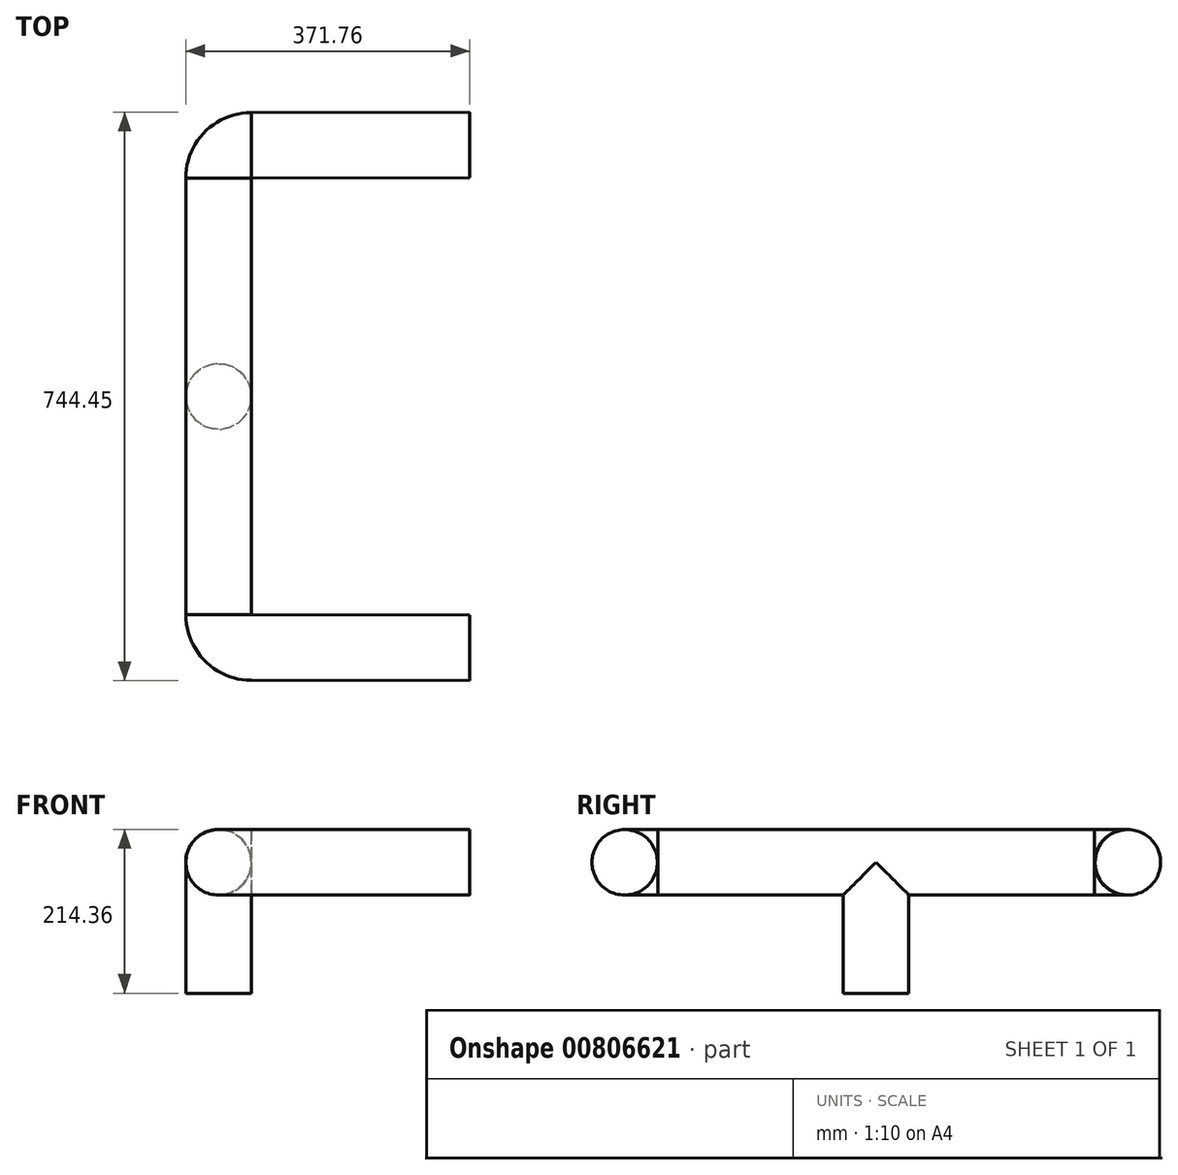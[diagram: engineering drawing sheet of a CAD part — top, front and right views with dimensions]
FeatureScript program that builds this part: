
annotation { "Feature Type Name" : "Feature", "Feature Type Description" : "" }
export const myFeature = defineFeature(function(context is Context, id is Id, definition is map)
    precondition{}
    {
        {
            var Q0;
            Q0=qCreatedBy(makeId("Top.planeOp"),FACE);
            var sketch = newSketch(context, id + "F0", { "sketchPlane" : qUnion([Q0])});
            skCircle(sketch, "E0", {"center": v(0, 0) * mm, "radius": 76.2 * mm});
            skSolve(sketch);
        }
        {
            var Q0;
            Q0=makeQuery(id+"F0.imprint","IMPRINT",FACE,{"disambiguationData":[TD([[makeQuery(id+"F0.imprint","IMPRINT",EDGE,{"derivedFrom":sQuery(id+"F0.wireOp",EDGE,"E0")}),1.0]])]});
            extrude(context, id + "F1", {"entities" : qUnion([Q0]), "depth" : 304.8 * mm, "offsetDistance" : 25.4 * mm});
        }
        {
            var Q0;
            Q0=makeQuery(id+"F1.opExtrude","CAP_FACE",FACE,{"disambiguationData":[OSD([sQuery(id+"F0.wireOp",EDGE,"E0")])],"isStart":false});
            var sketch = newSketch(context, id + "F2", { "sketchPlane" : qUnion([Q0])});
            skLineSegment(sketch, "E1", {"start": v(0, 0) * mm, "end": v(0, -508) * mm});
            skSolve(sketch);
        }
        {
            var Q0;
            Q0=makeQuery(id+"F2.imprint","IMPRINT",FACE,{"disambiguationData":[TD([[makeQuery(id+"F2.imprint","IMPRINT",EDGE,{"derivedFrom":makeQuery(id+"F1.opExtrude","CAP_EDGE",EDGE,{"disambiguationData":[OSD([sQuery(id+"F0.wireOp",EDGE,"E0")])],"isStart":false})}),1.0]])]});
            var sketch = newSketch(context, id + "F3", { "sketchPlane" : qUnion([Q0])});
            skLineSegment(sketch, "E2", {"start": v(0, 0) * mm, "end": v(0, 508) * mm});
            skSolve(sketch);
        }
        {
            var Q0;
            Q0=sQuery(id+"F2.wireOp",VERTEX,"E1.end");
            var Q1;
            Q1=sQuery(id+"F2.wireOp",EDGE,"E1");
            cPlane(context, id + "F4", {"entities" : qUnion([Q0, Q1]), "cplaneType" : CPlaneType.LINE_POINT, "offset" : 25.4 * mm, "width" : 152.4 * mm, "height" : 152.4 * mm});
        }
        {
            var Q0;
            Q0=qCreatedBy(id+"F4.planeOp",FACE);
            var sketch = newSketch(context, id + "F5", { "sketchPlane" : qUnion([Q0])});
            skPoint(sketch, "E3", {"position": v(0, 304.8) * mm});
            skSolve(sketch);
        }
        {
            var Q0;
            Q0=qCreatedBy(id+"F4.planeOp",FACE);
            var sketch = newSketch(context, id + "F6", { "sketchPlane" : qUnion([Q0])});
            skCircle(sketch, "E4", {"center": v(0, 304.89) * mm, "radius": 76.2 * mm});
            skSolve(sketch);
        }
        {
            var Q0;
            Q0=makeQuery(id+"F6.imprint","IMPRINT",FACE,{"disambiguationData":[TD([[makeQuery(id+"F6.imprint","IMPRINT",EDGE,{"derivedFrom":sQuery(id+"F6.wireOp",EDGE,"E4")}),1.0]])]});
            var Q1;
            Q1=sQuery(id+"F2.wireOp",EDGE,"E1");
            var Q2;
            Q2=sQuery(id+"F3.wireOp",EDGE,"E2");
            sweep(context, id + "F7", {"operationType" : NewBodyOperationType.ADD, "profiles" : qUnion([Q0]), "path" : qUnion([Q1, Q2])});
        }
        {
            var Q0;
            Q0=makeQuery(id+"F7.opSweep","CAP_FACE",FACE,{"disambiguationData":[OSD([sQuery(id+"F2.wireOp",VERTEX,"E1.end"),sQuery(id+"F6.wireOp",EDGE,"E4")])],"isStart":true});
            var sketch = newSketch(context, id + "F8", { "sketchPlane" : qUnion([Q0])});
            skLineSegment(sketch, "E5", {"start": v(0, 304.89) * mm, "end": v(0, 228.69) * mm});
            skSolve(sketch);
        }
        {
            var Q0;
            Q0=sQuery(id+"F8.wireOp",EDGE,"E5");
            var Q1;
            Q1=sQuery(id+"F5.wireOp",VERTEX,"E3");
            cPlane(context, id + "F9", {"entities" : qUnion([Q0, Q1]), "cplaneType" : CPlaneType.LINE_POINT, "offset" : 25.4 * mm, "width" : 152.4 * mm, "height" : 152.4 * mm});
        }
        {
            var Q0;
            Q0=qCreatedBy(id+"F9.planeOp",FACE);
            var sketch = newSketch(context, id + "F10", { "sketchPlane" : qUnion([Q0])});
            skArc(sketch, "E6", {"start": v(76.2, 584.23) * mm, "mid": v(22.4, 561.9) * mm, "end": v(0.07, 508.08) * mm});
            skSolve(sketch);
        }
        {
            var Q0;
            Q0=sQuery(id+"F10.wireOp",EDGE,"E6");
            var Q1;
            Q1=sQuery(id+"F10.wireOp",VERTEX,"E6.start");
            cPlane(context, id + "F11", {"entities" : qUnion([Q0, Q1]), "cplaneType" : CPlaneType.CURVE_POINT, "offset" : 25.4 * mm, "width" : 152.4 * mm, "height" : 152.4 * mm});
        }
        {
            var Q0;
            Q0=qCreatedBy(id+"F11.planeOp",FACE);
            var sketch = newSketch(context, id + "F12", { "sketchPlane" : qUnion([Q0])});
            skCircle(sketch, "E7", {"center": v(584.29, 304.8) * mm, "radius": 76.2 * mm});
            skSolve(sketch);
        }
        {
            var Q0;
            Q0=makeQuery(id+"F12.imprint","IMPRINT",FACE,{"disambiguationData":[TD([[makeQuery(id+"F12.imprint","IMPRINT",EDGE,{"derivedFrom":sQuery(id+"F12.wireOp",EDGE,"E7")}),1.0]])]});
            var Q1;
            Q1=sQuery(id+"F10.wireOp",EDGE,"E6");
            sweep(context, id + "F13", {"profiles" : qUnion([Q0]), "path" : qUnion([Q1])});
        }
        {
            var Q0;
            Q0=makeQuery(id+"F7.opSweep","CAP_FACE",FACE,{"disambiguationData":[OSD([sQuery(id+"F3.wireOp",VERTEX,"E2.end"),sQuery(id+"F6.wireOp",EDGE,"E4")])],"isStart":false});
            var sketch = newSketch(context, id + "F14", { "sketchPlane" : qUnion([Q0])});
            skPoint(sketch, "E8", {"position": v(0, 304.89) * mm});
            skSolve(sketch);
        }
        {
            var Q0;
            Q0=qCreatedBy(makeId("Right.planeOp"),FACE);
            var sketch = newSketch(context, id + "F15", { "sketchPlane" : qUnion([Q0])});
            skLineSegment(sketch, "E9", {"start": v(508.18, 305.03) * mm, "end": v(426.1, 305.03) * mm});
            skSolve(sketch);
        }
        {
            var Q0;
            Q0=sQuery(id+"F15.wireOp",EDGE,"E9");
            var Q1;
            Q1=sQuery(id+"F14.wireOp",VERTEX,"E8");
            cPlane(context, id + "F16", {"entities" : qUnion([Q0, Q1]), "cplaneType" : CPlaneType.LINE_POINT, "offset" : 25.4 * mm, "width" : 152.4 * mm, "height" : 152.4 * mm});
        }
        {
            var Q0;
            Q0=qCreatedBy(id+"F16.planeOp",FACE);
            var sketch = newSketch(context, id + "F17", { "sketchPlane" : qUnion([Q0])});
            skLineSegment(sketch, "E10", {"start": v(0, 306.54) * mm, "end": v(0, 229.61) * mm});
            skSolve(sketch);
        }
        {
            var Q0;
            Q0=sQuery(id+"F17.wireOp",EDGE,"E10");
            var Q1;
            Q1=sQuery(id+"F14.wireOp",VERTEX,"E8");
            cPlane(context, id + "F18", {"entities" : qUnion([Q0, Q1]), "cplaneType" : CPlaneType.LINE_POINT, "offset" : 25.4 * mm, "width" : 152.4 * mm, "height" : 152.4 * mm});
        }
        {
            var Q0;
            Q0=qCreatedBy(id+"F18.planeOp",FACE);
            var sketch = newSketch(context, id + "F19", { "sketchPlane" : qUnion([Q0])});
            skArc(sketch, "E11", {"start": v(0, -508.1) * mm, "mid": v(22.24, -561.88) * mm, "end": v(75.96, -584.27) * mm});
            skSolve(sketch);
        }
        {
            var Q0;
            Q0=sQuery(id+"F19.wireOp",EDGE,"E11");
            var Q1;
            Q1=sQuery(id+"F19.wireOp",VERTEX,"E11.end");
            cPlane(context, id + "F20", {"entities" : qUnion([Q0, Q1]), "cplaneType" : CPlaneType.CURVE_POINT, "offset" : 25.4 * mm, "width" : 152.4 * mm, "height" : 152.4 * mm});
        }
        {
            var Q0;
            Q0=qCreatedBy(id+"F20.planeOp",FACE);
            var sketch = newSketch(context, id + "F21", { "sketchPlane" : qUnion([Q0])});
            skCircle(sketch, "E12", {"center": v(584.46, 304.75) * mm, "radius": 76.2 * mm});
            skSolve(sketch);
        }
        {
            var Q0;
            Q0=makeQuery(id+"F21.imprint","IMPRINT",FACE,{"disambiguationData":[TD([[makeQuery(id+"F21.imprint","IMPRINT",EDGE,{"derivedFrom":sQuery(id+"F21.wireOp",EDGE,"E12")}),1.0]])]});
            var Q1;
            Q1=sQuery(id+"F19.wireOp",EDGE,"E11");
            sweep(context, id + "F22", {"profiles" : qUnion([Q0]), "path" : qUnion([Q1])});
        }
        {
            var Q0;
            Q0=makeQuery(id+"F13.opSweep","CAP_FACE",FACE,{"disambiguationData":[OSD([sQuery(id+"F10.wireOp",VERTEX,"E6.start"),sQuery(id+"F12.wireOp",EDGE,"E7")])],"isStart":true});
            var sketch = newSketch(context, id + "F23", { "sketchPlane" : qUnion([Q0])});
            skPoint(sketch, "E13", {"position": v(-584.29, 304.8) * mm});
            skSolve(sketch);
        }
        {
            var Q0;
            Q0=makeQuery(id+"F23.imprint","IMPRINT",FACE,{"disambiguationData":[TD([[makeQuery(id+"F23.imprint","IMPRINT",EDGE,{"derivedFrom":makeQuery(id+"F13.opSweep","CAP_EDGE",EDGE,{"disambiguationData":[OSD([sQuery(id+"F10.wireOp",VERTEX,"E6.start"),sQuery(id+"F12.wireOp",EDGE,"E7")])],"isStart":true})}),-1.0]])]});
            var sketch = newSketch(context, id + "F24", { "sketchPlane" : qUnion([Q0])});
            skCircle(sketch, "E14", {"center": v(-584.28, 304.81) * mm, "radius": 76.2 * mm});
            skSolve(sketch);
        }
        {
            var Q0;
            Q0 = qSketchRegion(id + "F24", true);
            extrude(context, id + "F25", {"entities" : qUnion([Q0]), "operationType" : NewBodyOperationType.ADD, "depth" : 508 * mm, "offsetDistance" : 25.4 * mm});
        }
        {
            var Q0;
            Q0=makeQuery(id+"F22.opSweep","CAP_FACE",FACE,{"disambiguationData":[OSD([sQuery(id+"F19.wireOp",VERTEX,"E11.end"),sQuery(id+"F21.wireOp",EDGE,"E12")])],"isStart":true});
            var sketch = newSketch(context, id + "F26", { "sketchPlane" : qUnion([Q0])});
            skPoint(sketch, "E15", {"position": v(584.46, 304.75) * mm});
            skSolve(sketch);
        }
        {
            var Q0;
            Q0=makeQuery(id+"F26.imprint","IMPRINT",FACE,{"disambiguationData":[TD([[makeQuery(id+"F26.imprint","IMPRINT",EDGE,{"derivedFrom":makeQuery(id+"F22.opSweep","CAP_EDGE",EDGE,{"disambiguationData":[OSD([sQuery(id+"F19.wireOp",VERTEX,"E11.end"),sQuery(id+"F21.wireOp",EDGE,"E12")])],"isStart":true})}),-1.0]])]});
            var sketch = newSketch(context, id + "F27", { "sketchPlane" : qUnion([Q0])});
            skCircle(sketch, "E16", {"center": v(584.45, 304.76) * mm, "radius": 76.2 * mm});
            skSolve(sketch);
        }
        {
            var Q0;
            Q0 = qSketchRegion(id + "F27", true);
            extrude(context, id + "F28", {"entities" : qUnion([Q0]), "operationType" : NewBodyOperationType.ADD, "depth" : 508 * mm, "offsetDistance" : 25.4 * mm});
        }
        {
            var Q0;
            Q0=makeQuery(id+"F13.opSweep","SWEPT_BODY",BODY,{"disambiguationData":[OSD([sQuery(id+"F10.wireOp",EDGE,"E6"),sQuery(id+"F12.wireOp",EDGE,"E7")])]});
            var Q1;
            Q1=makeQuery(id+"F1.opExtrude","SWEPT_BODY",BODY,{"disambiguationData":[OSD([sQuery(id+"F0.wireOp",EDGE,"E0")])]});
            var Q2;
            Q2=makeQuery(id+"F22.opSweep","SWEPT_BODY",BODY,{"disambiguationData":[OSD([sQuery(id+"F19.wireOp",EDGE,"E11"),sQuery(id+"F21.wireOp",EDGE,"E12")])]});
            var Q3;
            Q3=qCreatedBy(makeId("Origin.pointOp"),VERTEX);
            transform(context, id + "F29", {"entities" : qUnion([Q0, Q1, Q2]), "transformType" : TransformType.SCALE_UNIFORMLY, "scale" : .75, "scalePoint" : qUnion([Q3]), "makeCopy" : false});
        }
        {
            var Q0;
            Q0=makeQuery(id+"F13.opSweep","SWEPT_BODY",BODY,{"disambiguationData":[OSD([sQuery(id+"F10.wireOp",EDGE,"E6"),sQuery(id+"F12.wireOp",EDGE,"E7")])]});
            var Q1;
            Q1=makeQuery(id+"F1.opExtrude","SWEPT_BODY",BODY,{"disambiguationData":[OSD([sQuery(id+"F0.wireOp",EDGE,"E0")])]});
            var Q2;
            Q2=makeQuery(id+"F22.opSweep","SWEPT_BODY",BODY,{"disambiguationData":[OSD([sQuery(id+"F19.wireOp",EDGE,"E11"),sQuery(id+"F21.wireOp",EDGE,"E12")])]});
            var Q3;
            Q3=qCreatedBy(makeId("Origin.pointOp"),VERTEX);
            transform(context, id + "F30", {"entities" : qUnion([Q0, Q1, Q2]), "transformType" : TransformType.SCALE_UNIFORMLY, "scale" : .75, "scalePoint" : qUnion([Q3]), "makeCopy" : false});
        }
    });
